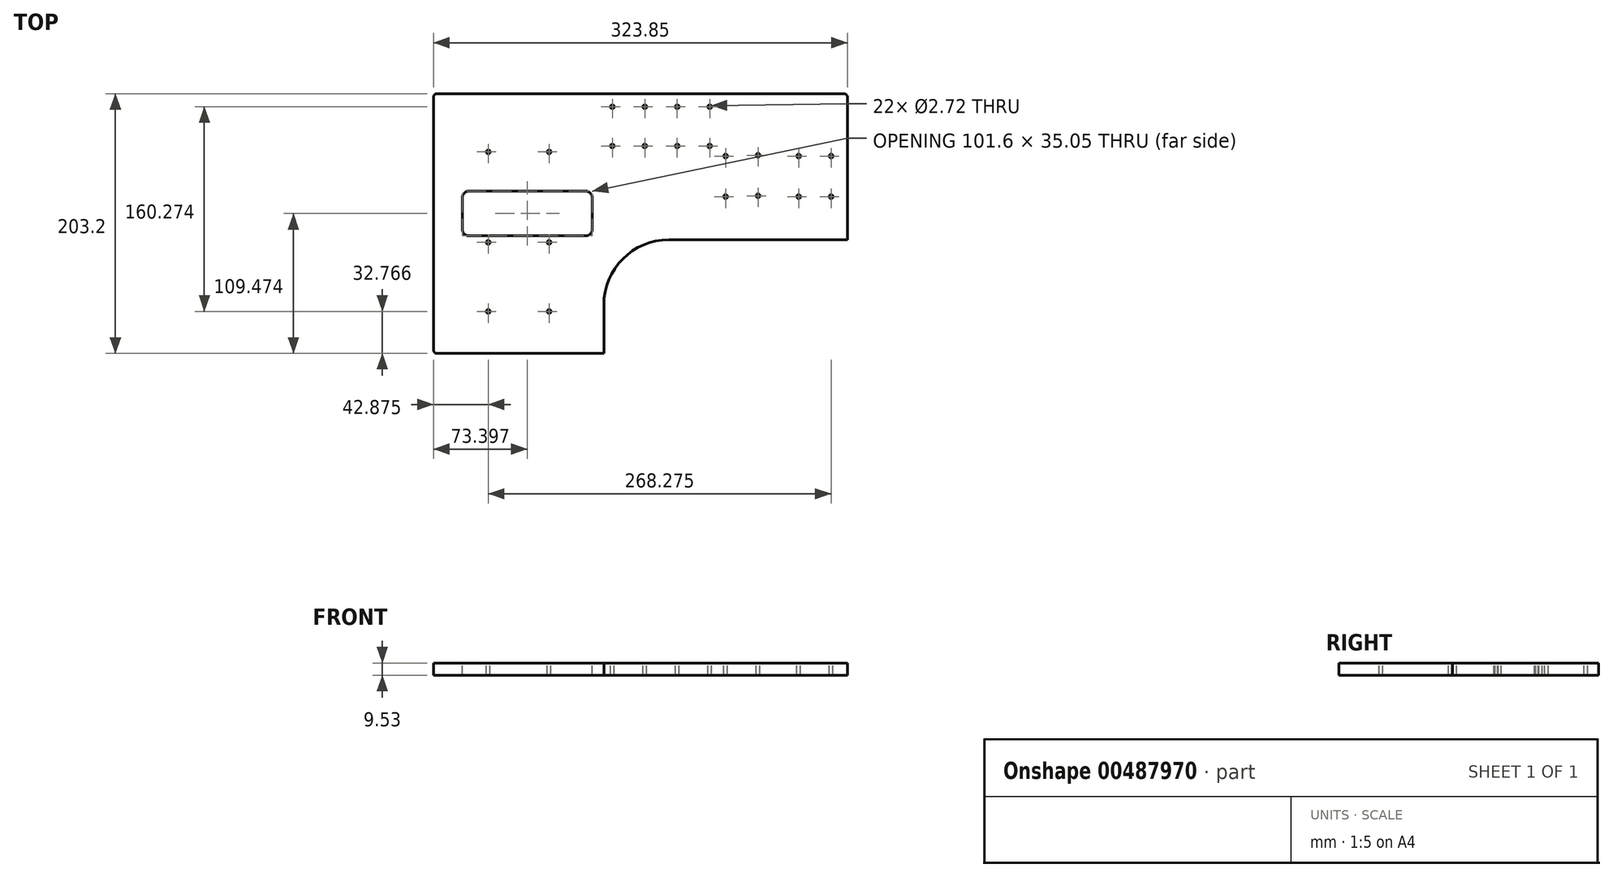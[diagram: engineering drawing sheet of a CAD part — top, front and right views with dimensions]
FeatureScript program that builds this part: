
annotation { "Feature Type Name" : "Feature", "Feature Type Description" : "" }
export const myFeature = defineFeature(function(context is Context, id is Id, definition is map)
    precondition{}
    {
        {
            var Q0;
            Q0=qCreatedBy(makeId("Top.planeOp"),FACE);
            var sketch = newSketch(context, id + "F0", { "sketchPlane" : qUnion([Q0])});
            skLineSegment(sketch, "E0.bottom", {"start": v(0, 0) * mm, "end": v(-323.85, 0) * mm});
            skLineSegment(sketch, "E0.top", {"start": v(0, 203.2) * mm, "end": v(-323.85, 203.2) * mm});
            skLineSegment(sketch, "E0.left", {"start": v(0, 0) * mm, "end": v(0, 203.2) * mm});
            skLineSegment(sketch, "E0.right", {"start": v(-323.85, 0) * mm, "end": v(-323.85, 203.2) * mm});
            skSolve(sketch);
        }
        {
            var Q0;
            Q0=makeQuery(id+"F0.imprint","IMPRINT",FACE,{"disambiguationData":[TD([[makeQuery(id+"F0.imprint","IMPRINT",EDGE,{"derivedFrom":sQuery(id+"F0.wireOp",EDGE,"E0.bottom")}),-1.0]])]});
            extrude(context, id + "F1", {"entities" : qUnion([Q0]), "depth" : 9.52 * mm});
        }
        {
            var Q0;
            Q0=makeQuery(id+"F1.opExtrude","SWEPT_EDGE",EDGE,{"disambiguationData":[OSD([sQuery(id+"F0.wireOp",EDGE,"E0.bottom"),sQuery(id+"F0.wireOp",EDGE,"E0.left")])]});
            var Q1;
            Q1=makeQuery(id+"F1.opExtrude","SWEPT_EDGE",EDGE,{"disambiguationData":[OSD([sQuery(id+"F0.wireOp",EDGE,"E0.top"),sQuery(id+"F0.wireOp",EDGE,"E0.left")])]});
            var Q2;
            Q2=makeQuery(id+"F1.opExtrude","SWEPT_EDGE",EDGE,{"disambiguationData":[OSD([sQuery(id+"F0.wireOp",EDGE,"E0.top"),sQuery(id+"F0.wireOp",EDGE,"E0.right")])]});
            var Q3;
            Q3=makeQuery(id+"F1.opExtrude","SWEPT_EDGE",EDGE,{"disambiguationData":[OSD([sQuery(id+"F0.wireOp",EDGE,"E0.bottom"),sQuery(id+"F0.wireOp",EDGE,"E0.right")])]});
            fillet(context, id + "F2", {"entities" : qUnion([Q0, Q1, Q2, Q3]), "radius" : 2.54 * mm, "tangentPropagation" : true, "allowEdgeOverflow" : false});
        }
        {
            var Q0;
            Q0=makeQuery(id+"F1.opExtrude","CAP_FACE",FACE,{"disambiguationData":[OSD([sQuery(id+"F0.wireOp",EDGE,"E0.bottom"),sQuery(id+"F0.wireOp",EDGE,"E0.top"),sQuery(id+"F0.wireOp",EDGE,"E0.left"),sQuery(id+"F0.wireOp",EDGE,"E0.right")])],"isStart":false});
            var sketch = newSketch(context, id + "F3", { "sketchPlane" : qUnion([Q0])});
            skPoint(sketch, "E1", {"position": v(-280.97, 157.73) * mm});
            skPoint(sketch, "E2", {"position": v(-233.35, 157.73) * mm});
            skPoint(sketch, "E3", {"position": v(-280.97, 86.87) * mm});
            skPoint(sketch, "E4", {"position": v(-233.35, 86.87) * mm});
            skPoint(sketch, "E5", {"position": v(-280.97, 32.77) * mm});
            skPoint(sketch, "E6", {"position": v(-233.35, 32.77) * mm});
            skPoint(sketch, "E7", {"position": v(-183.9, 193.04) * mm});
            skPoint(sketch, "E8", {"position": v(-158.5, 193.04) * mm});
            skPoint(sketch, "E9", {"position": v(-133.1, 193.04) * mm});
            skPoint(sketch, "E10", {"position": v(-107.7, 193.04) * mm});
            skPoint(sketch, "E11", {"position": v(-183.9, 162.3) * mm});
            skPoint(sketch, "E12", {"position": v(-158.5, 162.3) * mm});
            skPoint(sketch, "E13", {"position": v(-133.1, 162.3) * mm});
            skPoint(sketch, "E14", {"position": v(-107.7, 162.3) * mm});
            skPoint(sketch, "E15", {"position": v(-95.25, 154.43) * mm});
            skPoint(sketch, "E16", {"position": v(-95.25, 122.68) * mm});
            skPoint(sketch, "E17", {"position": v(-69.85, 123.35) * mm});
            skPoint(sketch, "E18", {"position": v(-69.86, 155.1) * mm});
            skPoint(sketch, "E19", {"position": v(-38.1, 154.43) * mm});
            skPoint(sketch, "E20", {"position": v(-38.1, 122.68) * mm});
            skPoint(sketch, "E21", {"position": v(-12.7, 122.68) * mm});
            skPoint(sketch, "E22", {"position": v(-12.7, 154.43) * mm});
            skSolve(sketch);
        }
        {
            var Q0;
            Q0=sQuery(id+"F3.wireOp",VERTEX,"E1");
            var Q1;
            Q1=sQuery(id+"F3.wireOp",VERTEX,"E2");
            var Q2;
            Q2=sQuery(id+"F3.wireOp",VERTEX,"E4");
            var Q3;
            Q3=sQuery(id+"F3.wireOp",VERTEX,"E3");
            var Q4;
            Q4=sQuery(id+"F3.wireOp",VERTEX,"E5");
            var Q5;
            Q5=sQuery(id+"F3.wireOp",VERTEX,"E6");
            var Q6;
            Q6=sQuery(id+"F3.wireOp",VERTEX,"E7");
            var Q7;
            Q7=sQuery(id+"F3.wireOp",VERTEX,"E8");
            var Q8;
            Q8=sQuery(id+"F3.wireOp",VERTEX,"E9");
            var Q9;
            Q9=sQuery(id+"F3.wireOp",VERTEX,"E10");
            var Q10;
            Q10=sQuery(id+"F3.wireOp",VERTEX,"E14");
            var Q11;
            Q11=sQuery(id+"F3.wireOp",VERTEX,"E13");
            var Q12;
            Q12=sQuery(id+"F3.wireOp",VERTEX,"E12");
            var Q13;
            Q13=sQuery(id+"F3.wireOp",VERTEX,"E11");
            var Q14;
            Q14=sQuery(id+"F3.wireOp",VERTEX,"E15");
            var Q15;
            Q15=sQuery(id+"F3.wireOp",VERTEX,"E16");
            var Q16;
            Q16=sQuery(id+"F3.wireOp",VERTEX,"E18");
            var Q17;
            Q17=sQuery(id+"F3.wireOp",VERTEX,"E17");
            var Q18;
            Q18=sQuery(id+"F3.wireOp",VERTEX,"E19");
            var Q19;
            Q19=sQuery(id+"F3.wireOp",VERTEX,"E20");
            var Q20;
            Q20=sQuery(id+"F3.wireOp",VERTEX,"E22");
            var Q21;
            Q21=sQuery(id+"F3.wireOp",VERTEX,"E21");
            var Q22;
            Q22=makeQuery(id+"F1.opExtrude","SWEPT_BODY",BODY,{"disambiguationData":[OSD([sQuery(id+"F0.wireOp",EDGE,"E0.bottom"),sQuery(id+"F0.wireOp",EDGE,"E0.top"),sQuery(id+"F0.wireOp",EDGE,"E0.left"),sQuery(id+"F0.wireOp",EDGE,"E0.right")])]});
            hole(context, id + "F4", {"style" : HoleStyle.C_SINK, "endStyle" : HoleEndStyle.THROUGH, "holeDiameter" : 2.72 * mm, "cSinkDiameter" : 2.97 * mm, "cSinkAngle" : 82 * degree, "isTappedThrough" : true, "tappedDepth" : 12.7 * mm, "tapClearance" : 3, "locations" : qUnion([Q0, Q1, Q2, Q3, Q4, Q5, Q6, Q7, Q8, Q9, Q10, Q11, Q12, Q13, Q14, Q15, Q16, Q17, Q18, Q19, Q20, Q21]), "scope" : qUnion([Q22])});
        }
        {
            var Q0;
            Q0=makeQuery(id+"F1.opExtrude","CAP_FACE",FACE,{"disambiguationData":[OSD([sQuery(id+"F0.wireOp",EDGE,"E0.bottom"),sQuery(id+"F0.wireOp",EDGE,"E0.top"),sQuery(id+"F0.wireOp",EDGE,"E0.left"),sQuery(id+"F0.wireOp",EDGE,"E0.right")])],"isStart":false});
            var sketch = newSketch(context, id + "F5", { "sketchPlane" : qUnion([Q0])});
            skLineSegment(sketch, "E23.bottom", {"start": v(-199.65, 91.95) * mm, "end": v(-301.25, 91.95) * mm});
            skLineSegment(sketch, "E23.top", {"start": v(-199.65, 127) * mm, "end": v(-301.25, 127) * mm});
            skLineSegment(sketch, "E23.left", {"start": v(-199.65, 91.95) * mm, "end": v(-199.65, 127) * mm});
            skLineSegment(sketch, "E23.right", {"start": v(-301.25, 91.95) * mm, "end": v(-301.25, 127) * mm});
            skSolve(sketch);
        }
        {
            var Q0;
            Q0=makeQuery(id+"F5.imprint","IMPRINT",FACE,{"disambiguationData":[TD([[makeQuery(id+"F5.imprint","IMPRINT",EDGE,{"derivedFrom":sQuery(id+"F5.wireOp",EDGE,"E23.bottom")}),-1.0]])]});
            extrude(context, id + "F6", {"entities" : qUnion([Q0]), "operationType" : NewBodyOperationType.REMOVE, "oppositeDirection" : true, "depth" : 25.4 * mm});
        }
        {
            var Q0;
            Q0=makeQuery(id+"F6.boolean.opBoolean","COPY",EDGE,{"derivedFrom":makeQuery(id+"F6.opExtrude","SWEPT_EDGE",EDGE,{"disambiguationData":[OSD([sQuery(id+"F5.wireOp",EDGE,"E23.bottom"),sQuery(id+"F5.wireOp",EDGE,"E23.right")])]})});
            var Q1;
            Q1=makeQuery(id+"F6.boolean.opBoolean","COPY",EDGE,{"derivedFrom":makeQuery(id+"F6.opExtrude","SWEPT_EDGE",EDGE,{"disambiguationData":[OSD([sQuery(id+"F5.wireOp",EDGE,"E23.top"),sQuery(id+"F5.wireOp",EDGE,"E23.right")])]})});
            var Q2;
            Q2=makeQuery(id+"F6.boolean.opBoolean","COPY",EDGE,{"derivedFrom":makeQuery(id+"F6.opExtrude","SWEPT_EDGE",EDGE,{"disambiguationData":[OSD([sQuery(id+"F5.wireOp",EDGE,"E23.top"),sQuery(id+"F5.wireOp",EDGE,"E23.left")])]})});
            var Q3;
            Q3=makeQuery(id+"F6.boolean.opBoolean","COPY",EDGE,{"derivedFrom":makeQuery(id+"F6.opExtrude","SWEPT_EDGE",EDGE,{"disambiguationData":[OSD([sQuery(id+"F5.wireOp",EDGE,"E23.bottom"),sQuery(id+"F5.wireOp",EDGE,"E23.left")])]})});
            fillet(context, id + "F7", {"entities" : qUnion([Q0, Q1, Q2, Q3]), "radius" : 5.08 * mm, "tangentPropagation" : true, "allowEdgeOverflow" : false});
        }
        {
            var Q0;
            Q0=makeQuery(id+"F1.opExtrude","CAP_FACE",FACE,{"disambiguationData":[OSD([sQuery(id+"F0.wireOp",EDGE,"E0.bottom"),sQuery(id+"F0.wireOp",EDGE,"E0.top"),sQuery(id+"F0.wireOp",EDGE,"E0.left"),sQuery(id+"F0.wireOp",EDGE,"E0.right")])],"isStart":false});
            var sketch = newSketch(context, id + "F8", { "sketchPlane" : qUnion([Q0])});
            skLineSegment(sketch, "E24.bottom", {"start": v(0, 0) * mm, "end": v(-190.5, 0) * mm});
            skLineSegment(sketch, "E24.top", {"start": v(0, 88.9) * mm, "end": v(-139.7, 88.9) * mm});
            skLineSegment(sketch, "E24.left", {"start": v(0, 0) * mm, "end": v(0, 88.9) * mm});
            skLineSegment(sketch, "E24.right", {"start": v(-190.5, 0) * mm, "end": v(-190.5, 38.1) * mm});
            skPoint(sketch, "E25.visualSharp", {"position": v(-190.5, 88.9) * mm});
            skArc(sketch, "E25.filletArc", {"start": v(-139.7, 88.9) * mm, "mid": v(-175.62, 74.02) * mm, "end": v(-190.5, 38.1) * mm});
            skSolve(sketch);
        }
        {
            var Q0;
            {var subQ4=sQuery(id+"F8.wireOp",EDGE,"E24.top");Q0=makeQuery(id+"F8.imprint","IMPRINT",FACE,{"disambiguationData":[TD([[makeQuery(id+"F8.imprint","IMPRINT",EDGE,{"derivedFrom":subQ4}),1.0]])]});}
            var sketch = newSketch(context, id + "F9", { "sketchPlane" : qUnion([Q0])});
            skLineSegment(sketch, "E26", {"start": v(-1.12, 11.57) * mm, "end": v(-58.27, 11.57) * mm});
            skLineSegment(sketch, "E27", {"start": v(-58.27, 11.57) * mm, "end": v(-58.27, 21.1) * mm});
            skLineSegment(sketch, "E28", {"start": v(-58.27, 21.1) * mm, "end": v(-48.75, 21.1) * mm});
            skLineSegment(sketch, "E29", {"start": v(-42.4, 27.44) * mm, "end": v(-42.4, 46.5) * mm});
            skLineSegment(sketch, "E30", {"start": v(-1.12, 11.57) * mm, "end": v(-1.12, 21.1) * mm});
            skLineSegment(sketch, "E31", {"start": v(-1.12, 21.1) * mm, "end": v(-10.65, 21.1) * mm});
            skLineSegment(sketch, "E32", {"start": v(-17, 27.44) * mm, "end": v(-17, 46.5) * mm});
            skArc(sketch, "E33", {"start": v(-17, 46.5) * mm, "mid": v(-29.7, 59.2) * mm, "end": v(-42.4, 46.5) * mm});
            skPoint(sketch, "E34.visualSharp", {"position": v(-42.4, 21.1) * mm});
            skArc(sketch, "E34.filletArc", {"start": v(-48.75, 21.1) * mm, "mid": v(-44.26, 22.95) * mm, "end": v(-42.4, 27.44) * mm});
            skPoint(sketch, "E35.visualSharp", {"position": v(-17, 21.1) * mm});
            skArc(sketch, "E35.filletArc", {"start": v(-17, 27.44) * mm, "mid": v(-15.14, 22.95) * mm, "end": v(-10.65, 21.1) * mm});
            skSolve(sketch);
        }
        {
            var Q0;
            Q0=sQuery(id+"F9.wireOp",VERTEX,"E33.center");
            var Q1;
            Q1=makeQuery(id+"F1.opExtrude","SWEPT_BODY",BODY,{"disambiguationData":[OSD([sQuery(id+"F0.wireOp",EDGE,"E0.bottom"),sQuery(id+"F0.wireOp",EDGE,"E0.top"),sQuery(id+"F0.wireOp",EDGE,"E0.left"),sQuery(id+"F0.wireOp",EDGE,"E0.right")])]});
            hole(context, id + "F10", {"style" : HoleStyle.SIMPLE, "endStyle" : HoleEndStyle.THROUGH, "holeDiameter" : 19.05 * mm, "isTappedThrough" : true, "tappedDepth" : 12.7 * mm, "tapClearance" : 3, "locations" : qUnion([Q0]), "scope" : qUnion([Q1])});
        }
        {
            var Q0;
            {var subQ4=sQuery(id+"F8.wireOp",EDGE,"E24.top");Q0=makeQuery(id+"F8.imprint","IMPRINT",FACE,{"disambiguationData":[TD([[makeQuery(id+"F8.imprint","IMPRINT",EDGE,{"derivedFrom":subQ4}),1.0]])]});}
            extrude(context, id + "F11", {"entities" : qUnion([Q0]), "operationType" : NewBodyOperationType.REMOVE, "oppositeDirection" : true, "depth" : 25.4 * mm, "offsetDistance" : 25.4 * mm});
        }
    });
